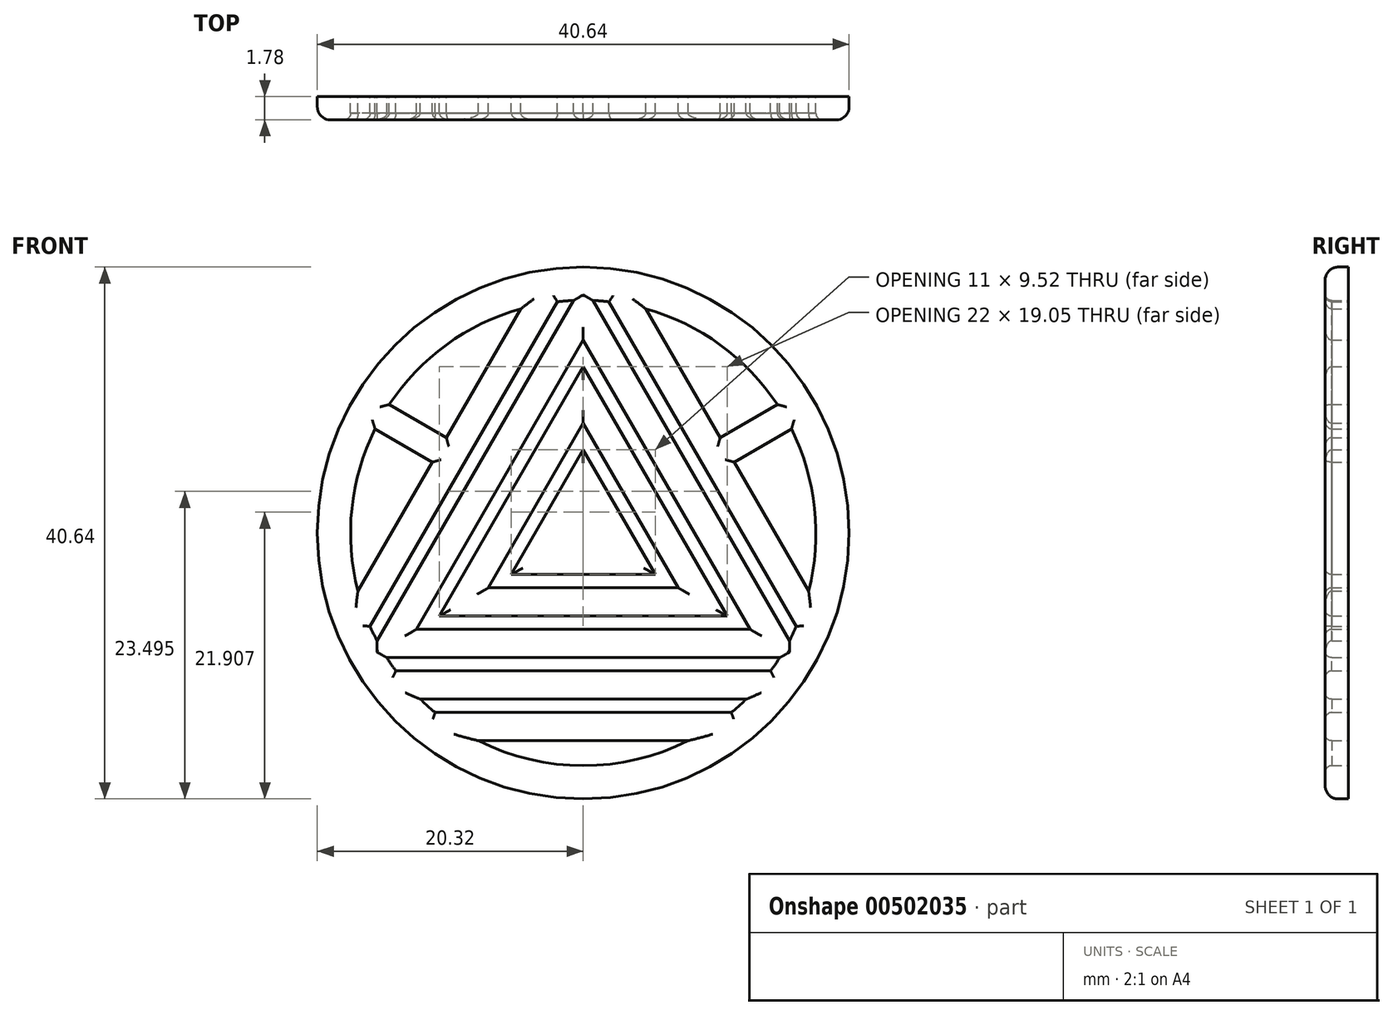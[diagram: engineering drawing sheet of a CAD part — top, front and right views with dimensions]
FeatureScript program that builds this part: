
annotation { "Feature Type Name" : "Feature", "Feature Type Description" : "" }
export const myFeature = defineFeature(function(context is Context, id is Id, definition is map)
    precondition{}
    {
        {
            var Q0;
            Q0=qCreatedBy(makeId("Front.planeOp"),FACE);
            var sketch = newSketch(context, id + "F0", { "sketchPlane" : qUnion([Q0])});
            skCircle(sketch, "E0", {"center": v(0, 0) * mm, "radius": 20.32 * mm});
            skCircle(sketch, "E1", {"center": v(0, 0) * mm, "radius": 17.78 * mm});
            skPoint(sketch, "E2", {"position": v(0, 6.35) * mm});
            skPoint(sketch, "E3", {"position": v(0, 8.38) * mm});
            skPoint(sketch, "E4", {"position": v(0, 12.7) * mm});
            skPoint(sketch, "E5", {"position": v(0, 14.73) * mm});
            skPoint(sketch, "E6", {"position": v(0, 19.05) * mm});
            skPoint(sketch, "E7", {"position": v(0, 21.08) * mm});
            skPoint(sketch, "E8", {"position": v(0, 23.88) * mm});
            skPoint(sketch, "E9.1.0", {"position": v(-5.5, -3.17) * mm});
            skPoint(sketch, "E9.1.1", {"position": v(-7.26, -4.2) * mm});
            skPoint(sketch, "E9.1.2", {"position": v(-11, -6.35) * mm});
            skPoint(sketch, "E9.1.3", {"position": v(-12.76, -7.37) * mm});
            skPoint(sketch, "E9.1.4", {"position": v(-16.5, -9.52) * mm});
            skPoint(sketch, "E9.1.5", {"position": v(-18.26, -10.54) * mm});
            skPoint(sketch, "E9.1.6", {"position": v(-20.68, -11.94) * mm});
            skPoint(sketch, "E9.2.0", {"position": v(5.5, -3.18) * mm});
            skPoint(sketch, "E9.2.1", {"position": v(7.26, -4.2) * mm});
            skPoint(sketch, "E9.2.2", {"position": v(11, -6.35) * mm});
            skPoint(sketch, "E9.2.3", {"position": v(12.76, -7.37) * mm});
            skPoint(sketch, "E9.2.4", {"position": v(16.5, -9.52) * mm});
            skPoint(sketch, "E9.2.5", {"position": v(18.26, -10.54) * mm});
            skPoint(sketch, "E9.2.6", {"position": v(20.68, -11.94) * mm});
            skLineSegment(sketch, "E10", {"start": v(0, 6.35) * mm, "end": v(-5.5, -3.17) * mm});
            skLineSegment(sketch, "E11", {"start": v(-5.5, -3.17) * mm, "end": v(5.5, -3.18) * mm});
            skLineSegment(sketch, "E12", {"start": v(5.5, -3.18) * mm, "end": v(0, 6.35) * mm});
            skLineSegment(sketch, "E13", {"start": v(0, 8.38) * mm, "end": v(-7.26, -4.2) * mm});
            skLineSegment(sketch, "E14", {"start": v(-7.26, -4.2) * mm, "end": v(7.26, -4.2) * mm});
            skLineSegment(sketch, "E15", {"start": v(7.26, -4.2) * mm, "end": v(0, 8.38) * mm});
            skLineSegment(sketch, "E16", {"start": v(0, 12.7) * mm, "end": v(-11, -6.35) * mm});
            skLineSegment(sketch, "E17", {"start": v(-11, -6.35) * mm, "end": v(11, -6.35) * mm});
            skLineSegment(sketch, "E18", {"start": v(11, -6.35) * mm, "end": v(0, 12.7) * mm});
            skLineSegment(sketch, "E19", {"start": v(0, 14.73) * mm, "end": v(-12.76, -7.37) * mm});
            skLineSegment(sketch, "E20", {"start": v(-12.76, -7.37) * mm, "end": v(12.76, -7.37) * mm});
            skLineSegment(sketch, "E21", {"start": v(12.76, -7.37) * mm, "end": v(0, 14.73) * mm});
            skLineSegment(sketch, "E22", {"start": v(-0.74, 17.76) * mm, "end": v(-15.76, -8.24) * mm});
            skLineSegment(sketch, "E23", {"start": v(0.74, 17.76) * mm, "end": v(15.76, -8.24) * mm});
            skLineSegment(sketch, "E24", {"start": v(15.01, -9.52) * mm, "end": v(-15.01, -9.52) * mm});
            skPoint(sketch, "E25", {"position": v(0, 25.9) * mm});
            skPoint(sketch, "E26", {"position": v(0, 29.72) * mm});
            skPoint(sketch, "E27.1.0", {"position": v(-22.44, -12.95) * mm});
            skPoint(sketch, "E27.1.1", {"position": v(-25.74, -14.86) * mm});
            skPoint(sketch, "E27.2.0", {"position": v(22.44, -12.95) * mm});
            skPoint(sketch, "E27.2.1", {"position": v(25.74, -14.86) * mm});
            skLineSegment(sketch, "E28.trimOffspring", {"start": v(16.29, -7.13) * mm, "end": v(1.97, 17.67) * mm});
            skLineSegment(sketch, "E29.trimOffspring", {"start": v(-14.32, -10.54) * mm, "end": v(14.32, -10.54) * mm});
            skLineSegment(sketch, "E30.trimOffspring", {"start": v(-16.29, -7.13) * mm, "end": v(-1.97, 17.67) * mm});
            skLineSegment(sketch, "E31.trimOffspring", {"start": v(17.22, -4.43) * mm, "end": v(4.78, 17.13) * mm});
            skLineSegment(sketch, "E32.trimOffspring", {"start": v(-4.78, 17.13) * mm, "end": v(-17.22, -4.43) * mm});
            skLineSegment(sketch, "E33.trimOffspring", {"start": v(-12.44, -12.7) * mm, "end": v(12.44, -12.7) * mm});
            skLineSegment(sketch, "E34.trimOffspring", {"start": v(-8, -15.88) * mm, "end": v(8, -15.88) * mm});
            skLineSegment(sketch, "E35.trimOffspring", {"start": v(-11.31, -13.72) * mm, "end": v(11.31, -13.72) * mm});
            skPoint(sketch, "E36", {"position": v(-11, 6.35) * mm});
            skPoint(sketch, "E37", {"position": v(11, 6.35) * mm});
            skLineSegment(sketch, "E38", {"start": v(-11.54, 5.42) * mm, "end": v(-15.9, 7.94) * mm});
            skLineSegment(sketch, "E39", {"start": v(-10.46, 7.28) * mm, "end": v(-14.83, 9.8) * mm});
            skLineSegment(sketch, "E40", {"start": v(10.46, 7.28) * mm, "end": v(14.83, 9.8) * mm});
            skLineSegment(sketch, "E41", {"start": v(11.54, 5.42) * mm, "end": v(15.9, 7.94) * mm});
            skSolve(sketch);
        }
        {
            var Q0;
            Q0 = qSketchRegion(id + "F0", true);
            var Q1;
            {var subQ0=sQuery(id+"F0.wireOp",EDGE,"E30.trimOffspring");Q1=makeQuery(id+"F0.imprint","IMPRINT",FACE,{"disambiguationData":[TD([[makeQuery(id+"F0.imprint","IMPRINT",EDGE,{"derivedFrom":subQ0}),1.0]])]});}
            var Q2;
            {var subQ0=sQuery(id+"F0.wireOp",EDGE,"E28.trimOffspring");Q2=makeQuery(id+"F0.imprint","IMPRINT",FACE,{"disambiguationData":[TD([[makeQuery(id+"F0.imprint","IMPRINT",EDGE,{"derivedFrom":subQ0}),-1.0]])]});}
            var Q3;
            {var subQ0=sQuery(id+"F0.wireOp",EDGE,"E29.trimOffspring");Q3=makeQuery(id+"F0.imprint","IMPRINT",FACE,{"disambiguationData":[TD([[makeQuery(id+"F0.imprint","IMPRINT",EDGE,{"derivedFrom":subQ0}),-1.0]])]});}
            var Q4;
            {var subQ0=sQuery(id+"F0.wireOp",EDGE,"E34.trimOffspring");Q4=makeQuery(id+"F0.imprint","IMPRINT",FACE,{"disambiguationData":[TD([[makeQuery(id+"F0.imprint","IMPRINT",EDGE,{"derivedFrom":subQ0}),1.0]])]});}
            var Q5;
            Q5=makeQuery(id+"F0.imprint","IMPRINT",FACE,{"disambiguationData":[TD([[makeQuery(id+"F0.imprint","IMPRINT",EDGE,{"derivedFrom":sQuery(id+"F0.wireOp",EDGE,"E19")}),-1.0]])]});
            var Q6;
            Q6=makeQuery(id+"F0.imprint","IMPRINT",FACE,{"disambiguationData":[TD([[makeQuery(id+"F0.imprint","IMPRINT",EDGE,{"derivedFrom":sQuery(id+"F0.wireOp",EDGE,"E13")}),-1.0]])]});
            var Q7;
            Q7=makeQuery(id+"F0.imprint","IMPRINT",FACE,{"disambiguationData":[TD([[makeQuery(id+"F0.imprint","IMPRINT",EDGE,{"derivedFrom":sQuery(id+"F0.wireOp",EDGE,"E10")}),1.0]])]});
            var Q8;
            {var subQ0=sQuery(id+"F0.wireOp",EDGE,"E38");Q8=makeQuery(id+"F0.imprint","IMPRINT",FACE,{"disambiguationData":[TD([[makeQuery(id+"F0.imprint","IMPRINT",EDGE,{"derivedFrom":subQ0}),-1.0]])]});}
            var Q9;
            {var subQ0=sQuery(id+"F0.wireOp",EDGE,"E40");Q9=makeQuery(id+"F0.imprint","IMPRINT",FACE,{"disambiguationData":[TD([[makeQuery(id+"F0.imprint","IMPRINT",EDGE,{"derivedFrom":subQ0}),-1.0]])]});}
            extrude(context, id + "F1", {"entities" : qUnion([Q0, Q1, Q2, Q3, Q4, Q5, Q6, Q7, Q8, Q9]), "depth" : 1.78 * mm, "offsetDistance" : 25.4 * mm});
        }
        {
            var Q0;
            Q0=makeQuery(id+"F1.opExtrude","CAP_EDGE",EDGE,{"disambiguationData":[OSD([sQuery(id+"F0.wireOp",EDGE,"E0")])],"isStart":false});
            fillet(context, id + "F2", {"entities" : qUnion([Q0]), "radius" : 1 * mm, "tangentPropagation" : true, "allowEdgeOverflow" : false});
        }
        {
            var Q0;
            {var subQ0=sQuery(id+"F0.wireOp",EDGE,"E1");Q0=makeQuery(id+"F1.opExtrude","CAP_EDGE",EDGE,{"disambiguationData":[OSD([subQ0]),TDD([makeQuery(id+"F0.imprint","IMPRINT",EDGE,{"disambiguationData":[TD([[makeQuery(id+"F0.imprint","INTERSECT",VERTEX,{"disambiguationData":[OD(0.0)],"derivedFrom":[subQ0,sQuery(id+"F0.wireOp",EDGE,"E32.trimOffspring")]}),-1.0]])],"derivedFrom":subQ0})])],"isStart":false});}
            var Q1;
            {var subQ0=sQuery(id+"F0.wireOp",EDGE,"E32.trimOffspring");Q1=makeQuery(id+"F1.opExtrude","CAP_EDGE",EDGE,{"disambiguationData":[OSD([subQ0]),TDD([makeQuery(id+"F0.imprint","IMPRINT",EDGE,{"disambiguationData":[TD([[makeQuery(id+"F0.imprint","INTERSECT",VERTEX,{"disambiguationData":[OD(0.0)],"derivedFrom":[sQuery(id+"F0.wireOp",EDGE,"E1"),subQ0]}),-1.0]])],"derivedFrom":subQ0})])],"isStart":false});}
            var Q2;
            Q2=makeQuery(id+"F1.opExtrude","CAP_EDGE",EDGE,{"disambiguationData":[OSD([sQuery(id+"F0.wireOp",EDGE,"E39")])],"isStart":false});
            var Q3;
            Q3=makeQuery(id+"F1.opExtrude","CAP_EDGE",EDGE,{"disambiguationData":[OSD([sQuery(id+"F0.wireOp",EDGE,"E38")])],"isStart":false});
            var Q4;
            {var subQ0=sQuery(id+"F0.wireOp",EDGE,"E1");Q4=makeQuery(id+"F1.opExtrude","CAP_EDGE",EDGE,{"disambiguationData":[OSD([subQ0]),TDD([makeQuery(id+"F0.imprint","IMPRINT",EDGE,{"disambiguationData":[TD([[makeQuery(id+"F0.imprint","INTERSECT",VERTEX,{"disambiguationData":[OD(1.0)],"derivedFrom":[subQ0,sQuery(id+"F0.wireOp",EDGE,"E32.trimOffspring")]}),1.0]])],"derivedFrom":subQ0})])],"isStart":false});}
            var Q5;
            {var subQ0=sQuery(id+"F0.wireOp",EDGE,"E32.trimOffspring");Q5=makeQuery(id+"F1.opExtrude","CAP_EDGE",EDGE,{"disambiguationData":[OSD([subQ0]),TDD([makeQuery(id+"F0.imprint","IMPRINT",EDGE,{"disambiguationData":[TD([[makeQuery(id+"F0.imprint","INTERSECT",VERTEX,{"disambiguationData":[OD(1.0)],"derivedFrom":[sQuery(id+"F0.wireOp",EDGE,"E1"),subQ0]}),1.0]])],"derivedFrom":subQ0})])],"isStart":false});}
            var Q6;
            {var subQ0=sQuery(id+"F0.wireOp",EDGE,"E1");Q6=makeQuery(id+"F1.opExtrude","CAP_EDGE",EDGE,{"disambiguationData":[OSD([subQ0]),TDD([makeQuery(id+"F0.imprint","IMPRINT",EDGE,{"disambiguationData":[TD([[makeQuery(id+"F0.imprint","INTERSECT",VERTEX,{"disambiguationData":[OD(0.0)],"derivedFrom":[subQ0,sQuery(id+"F0.wireOp",EDGE,"E22")]}),-1.0]])],"derivedFrom":subQ0})])],"isStart":false});}
            var Q7;
            {var subQ0=sQuery(id+"F0.wireOp",EDGE,"E1");Q7=makeQuery(id+"F1.opExtrude","CAP_EDGE",EDGE,{"disambiguationData":[OSD([subQ0]),TDD([makeQuery(id+"F0.imprint","IMPRINT",EDGE,{"disambiguationData":[TD([[makeQuery(id+"F0.imprint","INTERSECT",VERTEX,{"disambiguationData":[OD(0.0)],"derivedFrom":[subQ0,sQuery(id+"F0.wireOp",EDGE,"E23")]}),1.0]])],"derivedFrom":subQ0})])],"isStart":false});}
            var Q8;
            {var subQ0=sQuery(id+"F0.wireOp",EDGE,"E1");Q8=makeQuery(id+"F1.opExtrude","CAP_EDGE",EDGE,{"disambiguationData":[OSD([subQ0]),TDD([makeQuery(id+"F0.imprint","IMPRINT",EDGE,{"disambiguationData":[TD([[makeQuery(id+"F0.imprint","INTERSECT",VERTEX,{"disambiguationData":[OD(1.0)],"derivedFrom":[subQ0,sQuery(id+"F0.wireOp",EDGE,"E24")]}),-1.0]])],"derivedFrom":subQ0})])],"isStart":false});}
            var Q9;
            {var subQ0=sQuery(id+"F0.wireOp",EDGE,"E1");Q9=makeQuery(id+"F1.opExtrude","CAP_EDGE",EDGE,{"disambiguationData":[OSD([subQ0]),TDD([makeQuery(id+"F0.imprint","IMPRINT",EDGE,{"disambiguationData":[TD([[makeQuery(id+"F0.imprint","INTERSECT",VERTEX,{"disambiguationData":[OD(1.0)],"derivedFrom":[subQ0,sQuery(id+"F0.wireOp",EDGE,"E22")]}),1.0]])],"derivedFrom":subQ0})])],"isStart":false});}
            var Q10;
            {var subQ0=sQuery(id+"F0.wireOp",EDGE,"E1");Q10=makeQuery(id+"F1.opExtrude","CAP_EDGE",EDGE,{"disambiguationData":[OSD([subQ0]),TDD([makeQuery(id+"F0.imprint","IMPRINT",EDGE,{"disambiguationData":[TD([[makeQuery(id+"F0.imprint","INTERSECT",VERTEX,{"disambiguationData":[OD(1.0)],"derivedFrom":[subQ0,sQuery(id+"F0.wireOp",EDGE,"E23")]}),-1.0]])],"derivedFrom":subQ0})])],"isStart":false});}
            var Q11;
            {var subQ0=sQuery(id+"F0.wireOp",EDGE,"E1");Q11=makeQuery(id+"F1.opExtrude","CAP_EDGE",EDGE,{"disambiguationData":[OSD([subQ0]),TDD([makeQuery(id+"F0.imprint","IMPRINT",EDGE,{"disambiguationData":[TD([[makeQuery(id+"F0.imprint","INTERSECT",VERTEX,{"disambiguationData":[OD(0.0)],"derivedFrom":[subQ0,sQuery(id+"F0.wireOp",EDGE,"E24")]}),1.0]])],"derivedFrom":subQ0})])],"isStart":false});}
            var Q12;
            Q12=makeQuery(id+"F1.opExtrude","CAP_EDGE",EDGE,{"disambiguationData":[OSD([sQuery(id+"F0.wireOp",EDGE,"E30.trimOffspring")])],"isStart":false});
            var Q13;
            Q13=makeQuery(id+"F1.opExtrude","CAP_EDGE",EDGE,{"disambiguationData":[OSD([sQuery(id+"F0.wireOp",EDGE,"E22")])],"isStart":false});
            var Q14;
            Q14=makeQuery(id+"F1.opExtrude","CAP_EDGE",EDGE,{"disambiguationData":[OSD([sQuery(id+"F0.wireOp",EDGE,"E19")])],"isStart":false});
            var Q15;
            Q15=makeQuery(id+"F1.opExtrude","CAP_EDGE",EDGE,{"disambiguationData":[OSD([sQuery(id+"F0.wireOp",EDGE,"E16")])],"isStart":false});
            var Q16;
            Q16=makeQuery(id+"F1.opExtrude","CAP_EDGE",EDGE,{"disambiguationData":[OSD([sQuery(id+"F0.wireOp",EDGE,"E13")])],"isStart":false});
            var Q17;
            Q17=makeQuery(id+"F1.opExtrude","CAP_EDGE",EDGE,{"disambiguationData":[OSD([sQuery(id+"F0.wireOp",EDGE,"E10")])],"isStart":false});
            var Q18;
            {var subQ0=sQuery(id+"F0.wireOp",EDGE,"E31.trimOffspring");Q18=makeQuery(id+"F1.opExtrude","CAP_EDGE",EDGE,{"disambiguationData":[OSD([subQ0]),TDD([makeQuery(id+"F0.imprint","IMPRINT",EDGE,{"disambiguationData":[TD([[makeQuery(id+"F0.imprint","INTERSECT",VERTEX,{"disambiguationData":[OD(1.0)],"derivedFrom":[sQuery(id+"F0.wireOp",EDGE,"E1"),subQ0]}),1.0]])],"derivedFrom":subQ0})])],"isStart":false});}
            var Q19;
            {var subQ0=sQuery(id+"F0.wireOp",EDGE,"E1");Q19=makeQuery(id+"F1.opExtrude","CAP_EDGE",EDGE,{"disambiguationData":[OSD([subQ0]),TDD([makeQuery(id+"F0.imprint","IMPRINT",EDGE,{"disambiguationData":[TD([[makeQuery(id+"F0.imprint","INTERSECT",VERTEX,{"disambiguationData":[OD(1.0)],"derivedFrom":[subQ0,sQuery(id+"F0.wireOp",EDGE,"E31.trimOffspring")]}),1.0]])],"derivedFrom":subQ0})])],"isStart":false});}
            var Q20;
            Q20=makeQuery(id+"F1.opExtrude","CAP_EDGE",EDGE,{"disambiguationData":[OSD([sQuery(id+"F0.wireOp",EDGE,"E40")])],"isStart":false});
            var Q21;
            {var subQ0=sQuery(id+"F0.wireOp",EDGE,"E1");Q21=makeQuery(id+"F1.opExtrude","CAP_EDGE",EDGE,{"disambiguationData":[OSD([subQ0]),TDD([makeQuery(id+"F0.imprint","IMPRINT",EDGE,{"disambiguationData":[TD([[makeQuery(id+"F0.imprint","INTERSECT",VERTEX,{"disambiguationData":[OD(0.0)],"derivedFrom":[subQ0,sQuery(id+"F0.wireOp",EDGE,"E31.trimOffspring")]}),-1.0]])],"derivedFrom":subQ0})])],"isStart":false});}
            var Q22;
            Q22=makeQuery(id+"F1.opExtrude","CAP_EDGE",EDGE,{"disambiguationData":[OSD([sQuery(id+"F0.wireOp",EDGE,"E41")])],"isStart":false});
            var Q23;
            {var subQ0=sQuery(id+"F0.wireOp",EDGE,"E31.trimOffspring");Q23=makeQuery(id+"F1.opExtrude","CAP_EDGE",EDGE,{"disambiguationData":[OSD([subQ0]),TDD([makeQuery(id+"F0.imprint","IMPRINT",EDGE,{"disambiguationData":[TD([[makeQuery(id+"F0.imprint","INTERSECT",VERTEX,{"disambiguationData":[OD(0.0)],"derivedFrom":[sQuery(id+"F0.wireOp",EDGE,"E1"),subQ0]}),-1.0]])],"derivedFrom":subQ0})])],"isStart":false});}
            var Q24;
            Q24=makeQuery(id+"F1.opExtrude","CAP_EDGE",EDGE,{"disambiguationData":[OSD([sQuery(id+"F0.wireOp",EDGE,"E28.trimOffspring")])],"isStart":false});
            var Q25;
            Q25=makeQuery(id+"F1.opExtrude","CAP_EDGE",EDGE,{"disambiguationData":[OSD([sQuery(id+"F0.wireOp",EDGE,"E23")])],"isStart":false});
            var Q26;
            Q26=makeQuery(id+"F1.opExtrude","CAP_EDGE",EDGE,{"disambiguationData":[OSD([sQuery(id+"F0.wireOp",EDGE,"E21")])],"isStart":false});
            var Q27;
            Q27=makeQuery(id+"F1.opExtrude","CAP_EDGE",EDGE,{"disambiguationData":[OSD([sQuery(id+"F0.wireOp",EDGE,"E18")])],"isStart":false});
            var Q28;
            Q28=makeQuery(id+"F1.opExtrude","CAP_EDGE",EDGE,{"disambiguationData":[OSD([sQuery(id+"F0.wireOp",EDGE,"E12")])],"isStart":false});
            var Q29;
            Q29=makeQuery(id+"F1.opExtrude","CAP_EDGE",EDGE,{"disambiguationData":[OSD([sQuery(id+"F0.wireOp",EDGE,"E15")])],"isStart":false});
            var Q30;
            Q30=makeQuery(id+"F1.opExtrude","CAP_EDGE",EDGE,{"disambiguationData":[OSD([sQuery(id+"F0.wireOp",EDGE,"E11")])],"isStart":false});
            var Q31;
            Q31=makeQuery(id+"F1.opExtrude","CAP_EDGE",EDGE,{"disambiguationData":[OSD([sQuery(id+"F0.wireOp",EDGE,"E14")])],"isStart":false});
            var Q32;
            Q32=makeQuery(id+"F1.opExtrude","CAP_EDGE",EDGE,{"disambiguationData":[OSD([sQuery(id+"F0.wireOp",EDGE,"E17")])],"isStart":false});
            var Q33;
            Q33=makeQuery(id+"F1.opExtrude","CAP_EDGE",EDGE,{"disambiguationData":[OSD([sQuery(id+"F0.wireOp",EDGE,"E20")])],"isStart":false});
            var Q34;
            Q34=makeQuery(id+"F1.opExtrude","CAP_EDGE",EDGE,{"disambiguationData":[OSD([sQuery(id+"F0.wireOp",EDGE,"E24")])],"isStart":false});
            var Q35;
            Q35=makeQuery(id+"F1.opExtrude","CAP_EDGE",EDGE,{"disambiguationData":[OSD([sQuery(id+"F0.wireOp",EDGE,"E29.trimOffspring")])],"isStart":false});
            var Q36;
            Q36=makeQuery(id+"F1.opExtrude","CAP_EDGE",EDGE,{"disambiguationData":[OSD([sQuery(id+"F0.wireOp",EDGE,"E33.trimOffspring")])],"isStart":false});
            var Q37;
            Q37=makeQuery(id+"F1.opExtrude","CAP_EDGE",EDGE,{"disambiguationData":[OSD([sQuery(id+"F0.wireOp",EDGE,"E35.trimOffspring")])],"isStart":false});
            var Q38;
            Q38=makeQuery(id+"F1.opExtrude","CAP_EDGE",EDGE,{"disambiguationData":[OSD([sQuery(id+"F0.wireOp",EDGE,"E34.trimOffspring")])],"isStart":false});
            var Q39;
            {var subQ0=sQuery(id+"F0.wireOp",EDGE,"E34.trimOffspring");var subQ1=sQuery(id+"F0.wireOp",EDGE,"E1");Q39=makeQuery(id+"F1.opExtrude","CAP_EDGE",EDGE,{"disambiguationData":[OSD([subQ1]),TDD([makeQuery(id+"F0.imprint","IMPRINT",EDGE,{"disambiguationData":[TD([[makeQuery(id+"F0.imprint","INTERSECT",VERTEX,{"disambiguationData":[OD(0.0)],"derivedFrom":[subQ1,subQ0]}),-1.0]])],"derivedFrom":subQ1})])],"isStart":false});}
            var Q40;
            {var subQ0=sQuery(id+"F0.wireOp",EDGE,"E1");Q40=makeQuery(id+"F1.opExtrude","CAP_EDGE",EDGE,{"disambiguationData":[OSD([subQ0]),TDD([makeQuery(id+"F0.imprint","IMPRINT",EDGE,{"disambiguationData":[TD([[makeQuery(id+"F0.imprint","INTERSECT",VERTEX,{"disambiguationData":[OD(0.0)],"derivedFrom":[subQ0,sQuery(id+"F0.wireOp",EDGE,"E33.trimOffspring")]}),-1.0]])],"derivedFrom":subQ0})])],"isStart":false});}
            var Q41;
            {var subQ0=sQuery(id+"F0.wireOp",EDGE,"E1");Q41=makeQuery(id+"F1.opExtrude","CAP_EDGE",EDGE,{"disambiguationData":[OSD([subQ0]),TDD([makeQuery(id+"F0.imprint","IMPRINT",EDGE,{"disambiguationData":[TD([[makeQuery(id+"F0.imprint","INTERSECT",VERTEX,{"disambiguationData":[OD(1.0)],"derivedFrom":[subQ0,sQuery(id+"F0.wireOp",EDGE,"E33.trimOffspring")]}),1.0]])],"derivedFrom":subQ0})])],"isStart":false});}
            fillet(context, id + "F3", {"entities" : qUnion([Q0, Q1, Q2, Q3, Q4, Q5, Q6, Q7, Q8, Q9, Q10, Q11, Q12, Q13, Q14, Q15, Q16, Q17, Q18, Q19, Q20, Q21, Q22, Q23, Q24, Q25, Q26, Q27, Q28, Q29, Q30, Q31, Q32, Q33, Q34, Q35, Q36, Q37, Q38, Q39, Q40, Q41]), "radius" : 0.5 * mm, "tangentPropagation" : true, "allowEdgeOverflow" : false});
        }
        {
            var Q0;
            {var subQ3=sQuery(id+"F0.wireOp",EDGE,"E38");Q0=makeQuery(id+"F0.imprint","IMPRINT",FACE,{"disambiguationData":[TD([[makeQuery(id+"F0.imprint","IMPRINT",EDGE,{"derivedFrom":subQ3}),1.0]])]});}
            var Q1;
            {var subQ3=sQuery(id+"F0.wireOp",EDGE,"E39");Q1=makeQuery(id+"F0.imprint","IMPRINT",FACE,{"disambiguationData":[TD([[makeQuery(id+"F0.imprint","IMPRINT",EDGE,{"derivedFrom":subQ3}),-1.0]])]});}
            var Q2;
            {var subQ0=sQuery(id+"F0.wireOp",EDGE,"E22");Q2=makeQuery(id+"F0.imprint","IMPRINT",FACE,{"disambiguationData":[TD([[makeQuery(id+"F0.imprint","IMPRINT",EDGE,{"derivedFrom":subQ0}),-1.0]])]});}
            var Q3;
            Q3=makeQuery(id+"F0.imprint","IMPRINT",FACE,{"disambiguationData":[TD([[makeQuery(id+"F0.imprint","IMPRINT",EDGE,{"derivedFrom":sQuery(id+"F0.wireOp",EDGE,"E16")}),-1.0]])]});
            var Q4;
            {var subQ0=sQuery(id+"F0.wireOp",EDGE,"E23");Q4=makeQuery(id+"F0.imprint","IMPRINT",FACE,{"disambiguationData":[TD([[makeQuery(id+"F0.imprint","IMPRINT",EDGE,{"derivedFrom":subQ0}),1.0]])]});}
            var Q5;
            {var subQ3=sQuery(id+"F0.wireOp",EDGE,"E40");Q5=makeQuery(id+"F0.imprint","IMPRINT",FACE,{"disambiguationData":[TD([[makeQuery(id+"F0.imprint","IMPRINT",EDGE,{"derivedFrom":subQ3}),1.0]])]});}
            var Q6;
            {var subQ3=sQuery(id+"F0.wireOp",EDGE,"E41");Q6=makeQuery(id+"F0.imprint","IMPRINT",FACE,{"disambiguationData":[TD([[makeQuery(id+"F0.imprint","IMPRINT",EDGE,{"derivedFrom":subQ3}),-1.0]])]});}
            var Q7;
            Q7=makeQuery(id+"F0.imprint","IMPRINT",FACE,{"disambiguationData":[TD([[makeQuery(id+"F0.imprint","IMPRINT",EDGE,{"derivedFrom":sQuery(id+"F0.wireOp",EDGE,"E10")}),-1.0]])]});
            var Q8;
            {var subQ0=sQuery(id+"F0.wireOp",EDGE,"E24");Q8=makeQuery(id+"F0.imprint","IMPRINT",FACE,{"disambiguationData":[TD([[makeQuery(id+"F0.imprint","IMPRINT",EDGE,{"derivedFrom":subQ0}),1.0]])]});}
            var Q9;
            {var subQ0=sQuery(id+"F0.wireOp",EDGE,"E33.trimOffspring");Q9=makeQuery(id+"F0.imprint","IMPRINT",FACE,{"disambiguationData":[TD([[makeQuery(id+"F0.imprint","IMPRINT",EDGE,{"derivedFrom":subQ0}),-1.0]])]});}
            var Q10;
            {var subQ0=sQuery(id+"F0.wireOp",EDGE,"E34.trimOffspring");Q10=makeQuery(id+"F0.imprint","IMPRINT",FACE,{"disambiguationData":[TD([[makeQuery(id+"F0.imprint","IMPRINT",EDGE,{"derivedFrom":subQ0}),-1.0]])]});}
            extrude(context, id + "F4", {"entities" : qUnion([Q0, Q1, Q2, Q3, Q4, Q5, Q6, Q7, Q8, Q9, Q10]), "depth" : 1.27 * mm, "offsetDistance" : 25.4 * mm});
        }
    });
